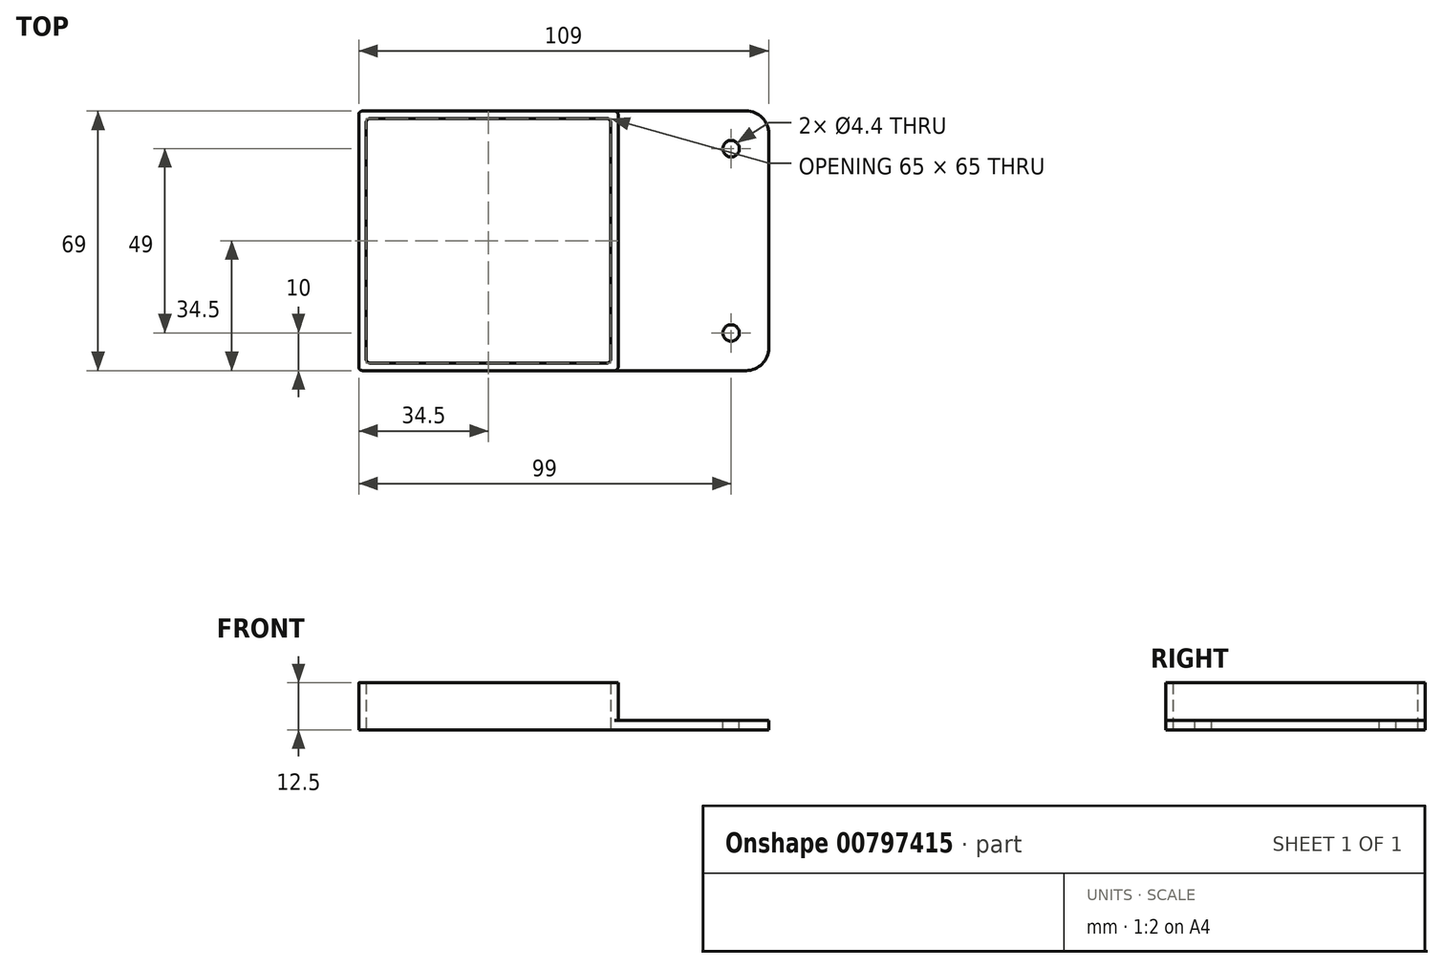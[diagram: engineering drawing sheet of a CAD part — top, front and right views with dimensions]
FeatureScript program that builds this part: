
annotation { "Feature Type Name" : "Feature", "Feature Type Description" : "" }
export const myFeature = defineFeature(function(context is Context, id is Id, definition is map)
    precondition{}
    {
        {
            var Q0;
            Q0=qCreatedBy(makeId("Top.planeOp"),FACE);
            var sketch = newSketch(context, id + "F0", { "sketchPlane" : qUnion([Q0])});
            skLineSegment(sketch, "E0.bottom", {"start": v(32.5, 32.5) * mm, "end": v(-32.5, 32.5) * mm});
            skLineSegment(sketch, "E0.top", {"start": v(32.5, -32.5) * mm, "end": v(-32.5, -32.5) * mm});
            skLineSegment(sketch, "E0.left", {"start": v(32.5, 32.5) * mm, "end": v(32.5, -32.5) * mm});
            skLineSegment(sketch, "E0.right", {"start": v(-32.5, 32.5) * mm, "end": v(-32.5, -32.5) * mm});
            skPoint(sketch, "E0.middle", {"position": v(0, 0) * mm});
            skLineSegment(sketch, "E1.0", {"start": v(34.5, -34.5) * mm, "end": v(-34.5, -34.5) * mm});
            skLineSegment(sketch, "E1.1", {"start": v(34.5, 34.5) * mm, "end": v(34.5, -34.5) * mm});
            skLineSegment(sketch, "E1.2", {"start": v(34.5, 34.5) * mm, "end": v(-34.5, 34.5) * mm});
            skLineSegment(sketch, "E1.3", {"start": v(-34.5, 34.5) * mm, "end": v(-34.5, -34.5) * mm});
            skLineSegment(sketch, "E2.bottom", {"start": v(34.5, 34.5) * mm, "end": v(74.5, 34.5) * mm});
            skLineSegment(sketch, "E2.top", {"start": v(34.5, -34.5) * mm, "end": v(74.5, -34.5) * mm});
            skLineSegment(sketch, "E2.right", {"start": v(74.5, 34.5) * mm, "end": v(74.5, -34.5) * mm});
            skPoint(sketch, "E3", {"position": v(64.5, 24.5) * mm});
            skPoint(sketch, "E4", {"position": v(64.5, -24.5) * mm});
            skSolve(sketch);
        }
        {
            var Q0;
            Q0=makeQuery(id+"F0.imprint","IMPRINT",FACE,{"disambiguationData":[TD([[makeQuery(id+"F0.imprint","IMPRINT",EDGE,{"derivedFrom":sQuery(id+"F0.wireOp",EDGE,"E0.bottom")}),-1.0]])]});
            extrude(context, id + "F1", {"entities" : qUnion([Q0]), "depth" : 10 * mm, "offsetDistance" : 25 * mm});
        }
        {
            var Q0;
            Q0=makeQuery(id+"F0.imprint","IMPRINT",FACE,{"disambiguationData":[TD([[makeQuery(id+"F0.imprint","IMPRINT",EDGE,{"derivedFrom":sQuery(id+"F0.wireOp",EDGE,"E2.bottom")}),-1.0]])]});
            var Q1;
            Q1=makeQuery(id+"F0.imprint","IMPRINT",FACE,{"disambiguationData":[TD([[makeQuery(id+"F0.imprint","IMPRINT",EDGE,{"derivedFrom":sQuery(id+"F0.wireOp",EDGE,"E0.bottom")}),-1.0]])]});
            extrude(context, id + "F2", {"entities" : qUnion([Q0, Q1]), "operationType" : NewBodyOperationType.ADD, "oppositeDirection" : true, "depth" : 2.5 * mm, "offsetDistance" : 25 * mm});
        }
        {
            var Q0;
            {var subQ0=sQuery(id+"F0.wireOp",EDGE,"E0.left");var subQ1=sQuery(id+"F0.wireOp",EDGE,"E0.bottom");Q0=makeQuery(id+"F2.boolean.opBoolean","MERGE",EDGE,{"derivedFrom":[makeQuery(id+"F1.opExtrude","SWEPT_EDGE",EDGE,{"disambiguationData":[OSD([subQ1,subQ0])]}),makeQuery(id+"F2.opExtrude","SWEPT_EDGE",EDGE,{"disambiguationData":[OSD([subQ1,subQ0])]})]});}
            var Q1;
            {var subQ0=sQuery(id+"F0.wireOp",EDGE,"E0.right");var subQ1=sQuery(id+"F0.wireOp",EDGE,"E0.bottom");Q1=makeQuery(id+"F2.boolean.opBoolean","MERGE",EDGE,{"derivedFrom":[makeQuery(id+"F1.opExtrude","SWEPT_EDGE",EDGE,{"disambiguationData":[OSD([subQ1,subQ0])]}),makeQuery(id+"F2.opExtrude","SWEPT_EDGE",EDGE,{"disambiguationData":[OSD([subQ1,subQ0])]})]});}
            var Q2;
            {var subQ0=sQuery(id+"F0.wireOp",EDGE,"E0.right");var subQ1=sQuery(id+"F0.wireOp",EDGE,"E0.top");Q2=makeQuery(id+"F2.boolean.opBoolean","MERGE",EDGE,{"derivedFrom":[makeQuery(id+"F1.opExtrude","SWEPT_EDGE",EDGE,{"disambiguationData":[OSD([subQ1,subQ0])]}),makeQuery(id+"F2.opExtrude","SWEPT_EDGE",EDGE,{"disambiguationData":[OSD([subQ1,subQ0])]})]});}
            var Q3;
            {var subQ0=sQuery(id+"F0.wireOp",EDGE,"E0.left");var subQ1=sQuery(id+"F0.wireOp",EDGE,"E0.top");Q3=makeQuery(id+"F2.boolean.opBoolean","MERGE",EDGE,{"derivedFrom":[makeQuery(id+"F1.opExtrude","SWEPT_EDGE",EDGE,{"disambiguationData":[OSD([subQ1,subQ0])]}),makeQuery(id+"F2.opExtrude","SWEPT_EDGE",EDGE,{"disambiguationData":[OSD([subQ1,subQ0])]})]});}
            var Q4;
            {var subQ0=sQuery(id+"F0.wireOp",EDGE,"E1.3");var subQ1=sQuery(id+"F0.wireOp",EDGE,"E1.2");Q4=makeQuery(id+"F2.boolean.opBoolean","MERGE",EDGE,{"derivedFrom":[makeQuery(id+"F1.opExtrude","SWEPT_EDGE",EDGE,{"disambiguationData":[OSD([subQ1,subQ0])]}),makeQuery(id+"F2.opExtrude","SWEPT_EDGE",EDGE,{"disambiguationData":[OSD([subQ1,subQ0])]})]});}
            var Q5;
            {var subQ0=sQuery(id+"F0.wireOp",EDGE,"E1.3");var subQ1=sQuery(id+"F0.wireOp",EDGE,"E1.0");Q5=makeQuery(id+"F2.boolean.opBoolean","MERGE",EDGE,{"derivedFrom":[makeQuery(id+"F1.opExtrude","SWEPT_EDGE",EDGE,{"disambiguationData":[OSD([subQ1,subQ0])]}),makeQuery(id+"F2.opExtrude","SWEPT_EDGE",EDGE,{"disambiguationData":[OSD([subQ1,subQ0])]})]});}
            var Q6;
            Q6=makeQuery(id+"F1.opExtrude","SWEPT_EDGE",EDGE,{"disambiguationData":[OSD([sQuery(id+"F0.wireOp",EDGE,"E1.2"),sQuery(id+"F0.wireOp",EDGE,"E2.bottom"),sQuery(id+"F0.wireOp",EDGE,"E1.1")])]});
            var Q7;
            Q7=makeQuery(id+"F1.opExtrude","SWEPT_EDGE",EDGE,{"disambiguationData":[OSD([sQuery(id+"F0.wireOp",EDGE,"E1.0"),sQuery(id+"F0.wireOp",EDGE,"E2.top"),sQuery(id+"F0.wireOp",EDGE,"E1.1")])]});
            fillet(context, id + "F3", {"entities" : qUnion([Q0, Q1, Q2, Q3, Q4, Q5, Q6, Q7]), "radius" : 1 * mm, "tangentPropagation" : true, "allowEdgeOverflow" : false});
        }
        {
            var Q0;
            Q0=makeQuery(id+"F1.opExtrude","CAP_EDGE",EDGE,{"disambiguationData":[OSD([sQuery(id+"F0.wireOp",EDGE,"E1.1")])],"isStart":true});
            var Q1;
            Q1=makeQuery(id+"F2.opExtrude","SWEPT_EDGE",EDGE,{"disambiguationData":[OSD([sQuery(id+"F0.wireOp",EDGE,"E2.bottom"),sQuery(id+"F0.wireOp",EDGE,"E2.right")])]});
            var Q2;
            Q2=makeQuery(id+"F2.opExtrude","SWEPT_EDGE",EDGE,{"disambiguationData":[OSD([sQuery(id+"F0.wireOp",EDGE,"E2.top"),sQuery(id+"F0.wireOp",EDGE,"E2.right")])]});
            fillet(context, id + "F4", {"entities" : qUnion([Q0, Q1, Q2]), "radius" : 6 * mm, "tangentPropagation" : true, "allowEdgeOverflow" : false});
        }
        {
            var Q0;
            Q0=sQuery(id+"F0.wireOp",VERTEX,"E4");
            var Q1;
            Q1=sQuery(id+"F0.wireOp",VERTEX,"E3");
            var Q2;
            Q2=makeQuery(id+"F1.opExtrude","SWEPT_BODY",BODY,{"disambiguationData":[OSD([sQuery(id+"F0.wireOp",EDGE,"E0.bottom"),sQuery(id+"F0.wireOp",EDGE,"E0.top"),sQuery(id+"F0.wireOp",EDGE,"E0.left"),sQuery(id+"F0.wireOp",EDGE,"E0.right"),sQuery(id+"F0.wireOp",EDGE,"E1.0"),sQuery(id+"F0.wireOp",EDGE,"E1.2"),sQuery(id+"F0.wireOp",EDGE,"E1.3"),sQuery(id+"F0.wireOp",EDGE,"E1.1")])]});
            hole(context, id + "F5", {"style" : HoleStyle.SIMPLE, "endStyle" : HoleEndStyle.THROUGH, "standardTappedOrClearance" : lookupTablePath({ "standard" : "ISO", "fit" : "Normal", "size" : "M4", "type" : "Clearance" }), "standardBlindInLast" : lookupTablePath({ "fit" : "Standard", "standard" : "ISO", "size" : "M4", "type" : "Clearance" }), "holeDiameter" : 4.4 * mm, "majorDiameter" : 5 * mm, "isTappedThrough" : true, "tappedDepth" : 12 * mm, "tapClearance" : 3, "locations" : qUnion([Q0, Q1]), "scope" : qUnion([Q2])});
        }
    });
